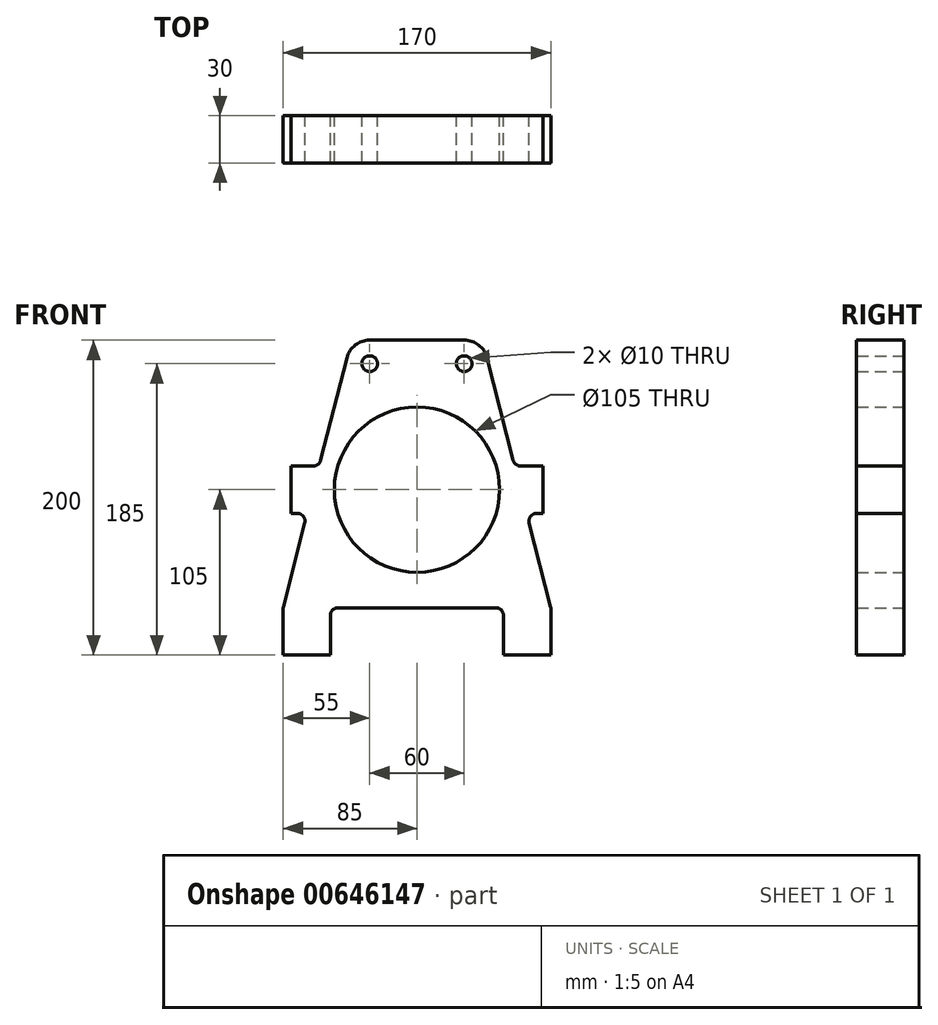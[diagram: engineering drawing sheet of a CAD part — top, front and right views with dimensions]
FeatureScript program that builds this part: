
annotation { "Feature Type Name" : "Feature", "Feature Type Description" : "" }
export const myFeature = defineFeature(function(context is Context, id is Id, definition is map)
    precondition{}
    {
        {
            var Q0;
            Q0=qCreatedBy(makeId("Front.planeOp"),FACE);
            var sketch = newSketch(context, id + "F0", { "sketchPlane" : qUnion([Q0])});
            skLineSegment(sketch, "E0", {"start": v(-85, 0) * mm, "end": v(-55, 0) * mm});
            skLineSegment(sketch, "E1", {"start": v(-55, 0) * mm, "end": v(-55, 30) * mm});
            skLineSegment(sketch, "E2", {"start": v(-55, 30) * mm, "end": v(-85, 30) * mm, "construction": true});
            skLineSegment(sketch, "E3", {"start": v(-85, 30) * mm, "end": v(-85, 0) * mm});
            skLineSegment(sketch, "E4", {"start": v(0, 0) * mm, "end": v(0, 185) * mm, "construction": true});
            skCircle(sketch, "E5", {"center": v(0, 105) * mm, "radius": 52.5 * mm, "construction": true});
            skLineSegment(sketch, "E6", {"start": v(-70, 0) * mm, "end": v(-70, 30) * mm, "construction": true});
            skCircle(sketch, "E7", {"center": v(-30, 185) * mm, "radius": 5 * mm});
            skLineSegment(sketch, "E8", {"start": v(-30, 185) * mm, "end": v(0, 185) * mm, "construction": true});
            skLineSegment(sketch, "E9", {"start": v(-55, 30) * mm, "end": v(0, 30) * mm});
            skArc(sketch, "E10.0.startCap", {"start": v(-30, 170) * mm, "mid": v(-45, 185) * mm, "end": v(-30, 200) * mm, "construction": true});
            skLineSegment(sketch, "E10.0.left", {"start": v(-30, 200) * mm, "end": v(0, 200) * mm, "construction": true});
            skLineSegment(sketch, "E10.0.right", {"start": v(-30, 170) * mm, "end": v(0, 170) * mm, "construction": true});
            skLineSegment(sketch, "E11", {"start": v(-85, 30) * mm, "end": v(-69.7, 90) * mm});
            skArc(sketch, "E12", {"start": v(-30, 200) * mm, "mid": v(-39.2, 196.84) * mm, "end": v(-44.53, 188.7) * mm});
            skLineSegment(sketch, "E13", {"start": v(-30, 200) * mm, "end": v(0, 200) * mm});
            skLineSegment(sketch, "E14.bottom", {"start": v(-80, 120) * mm, "end": v(0, 120) * mm, "construction": true});
            skLineSegment(sketch, "E14.top", {"start": v(-80, 90) * mm, "end": v(0, 90) * mm, "construction": true});
            skLineSegment(sketch, "E14.left", {"start": v(-80, 120) * mm, "end": v(-80, 90) * mm, "construction": true});
            skLineSegment(sketch, "E15.trimOffspring", {"start": v(-62.05, 120) * mm, "end": v(-44.53, 188.7) * mm});
            skLineSegment(sketch, "E16", {"start": v(-62.05, 120) * mm, "end": v(-69.7, 90) * mm, "construction": true});
            skLineSegment(sketch, "E17", {"start": v(0, 105) * mm, "end": v(-135.3, 105) * mm, "construction": true});
            skLineSegment(sketch, "E18", {"start": v(-62.05, 120) * mm, "end": v(-80, 120) * mm});
            skLineSegment(sketch, "E19", {"start": v(-80, 90) * mm, "end": v(-80, 120) * mm});
            skLineSegment(sketch, "E20", {"start": v(-80, 90) * mm, "end": v(-69.7, 90) * mm});
            skLineSegment(sketch, "E21", {"start": v(0, 200) * mm, "end": v(0, 157.5) * mm});
            skLineSegment(sketch, "E22", {"start": v(0, 52.5) * mm, "end": v(0, 30) * mm});
            skArc(sketch, "E23", {"start": v(0, 157.5) * mm, "mid": v(-52.5, 105) * mm, "end": v(0, 52.5) * mm});
            skSolve(sketch);
        }
        {
            var Q0;
            Q0=makeQuery(id+"F0.imprint","IMPRINT",FACE,{"disambiguationData":[TD([[makeQuery(id+"F0.imprint","IMPRINT",EDGE,{"derivedFrom":sQuery(id+"F0.wireOp",EDGE,"E0")}),1.0]])]});
            extrude(context, id + "F1", {"entities" : qUnion([Q0]), "depth" : 30 * mm, "offsetDistance" : 25 * mm, "symmetric" : true});
        }
        {
            var Q0;
            Q0=makeQuery(id+"F1.opExtrude","SWEPT_EDGE",EDGE,{"disambiguationData":[OSD([sQuery(id+"F0.wireOp",EDGE,"E11"),sQuery(id+"F0.wireOp",EDGE,"E20")])]});
            var Q1;
            Q1=makeQuery(id+"F1.opExtrude","SWEPT_EDGE",EDGE,{"disambiguationData":[OSD([sQuery(id+"F0.wireOp",EDGE,"E15.trimOffspring"),sQuery(id+"F0.wireOp",EDGE,"E18")])]});
            var Q2;
            Q2=makeQuery(id+"F1.opExtrude","SWEPT_EDGE",EDGE,{"disambiguationData":[OSD([sQuery(id+"F0.wireOp",EDGE,"E3"),sQuery(id+"F0.wireOp",EDGE,"E11")])]});
            var Q3;
            Q3=makeQuery(id+"F1.opExtrude","SWEPT_EDGE",EDGE,{"disambiguationData":[OSD([sQuery(id+"F0.wireOp",EDGE,"E1"),sQuery(id+"F0.wireOp",EDGE,"E9")])]});
            fillet(context, id + "F2", {"entities" : qUnion([Q0, Q1, Q2, Q3]), "radius" : 5 * mm, "tangentPropagation" : true, "allowEdgeOverflow" : false});
        }
        {
            var Q0;
            Q0=makeQuery(id+"F1.opExtrude","SWEPT_BODY",BODY,{"disambiguationData":[OSD([sQuery(id+"F0.wireOp",EDGE,"E0"),sQuery(id+"F0.wireOp",EDGE,"E1"),sQuery(id+"F0.wireOp",EDGE,"E3"),sQuery(id+"F0.wireOp",EDGE,"E7"),sQuery(id+"F0.wireOp",EDGE,"E9"),sQuery(id+"F0.wireOp",EDGE,"E11"),sQuery(id+"F0.wireOp",EDGE,"E12"),sQuery(id+"F0.wireOp",EDGE,"E13"),sQuery(id+"F0.wireOp",EDGE,"E15.trimOffspring"),sQuery(id+"F0.wireOp",EDGE,"E18"),sQuery(id+"F0.wireOp",EDGE,"E19"),sQuery(id+"F0.wireOp",EDGE,"E20"),sQuery(id+"F0.wireOp",EDGE,"E21"),sQuery(id+"F0.wireOp",EDGE,"E22"),sQuery(id+"F0.wireOp",EDGE,"E23")])]});
            var Q1;
            Q1=qCreatedBy(makeId("Right.planeOp"),FACE);
            mirror(context, id + "F3", {"operationType" : NewBodyOperationType.ADD, "entities" : qUnion([Q0]), "mirrorPlane" : qUnion([Q1])});
        }
    });
